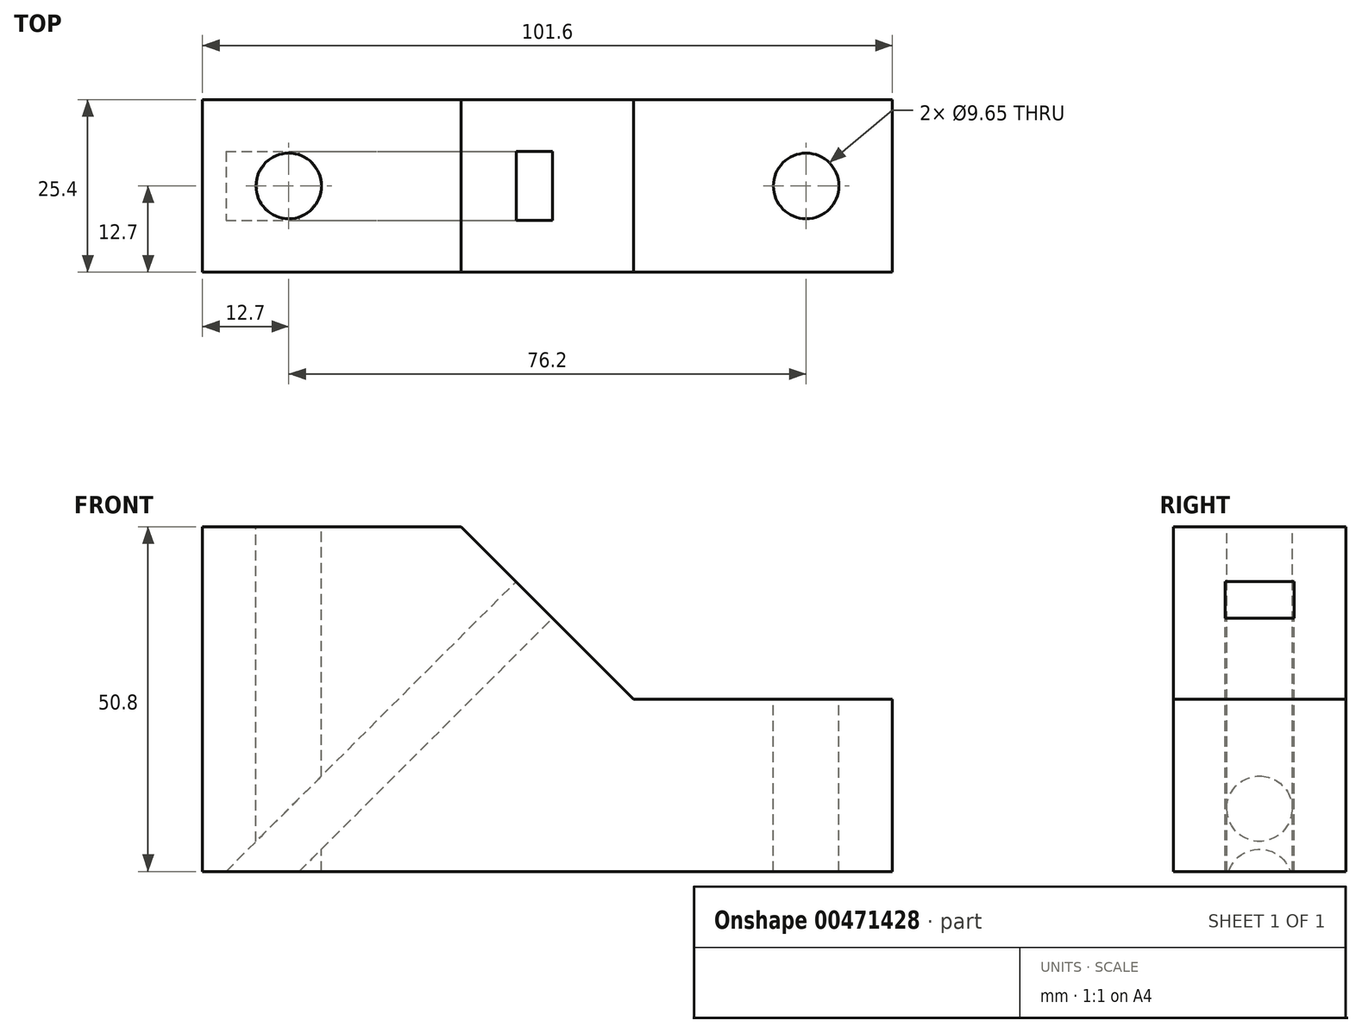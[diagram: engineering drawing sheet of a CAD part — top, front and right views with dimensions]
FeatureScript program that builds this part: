
annotation { "Feature Type Name" : "Feature", "Feature Type Description" : "" }
export const myFeature = defineFeature(function(context is Context, id is Id, definition is map)
    precondition{}
    {
        {
            var Q0;
            Q0=qCreatedBy(makeId("Front.planeOp"),FACE);
            var sketch = newSketch(context, id + "F0", { "sketchPlane" : qUnion([Q0])});
            skLineSegment(sketch, "E0", {"start": v(0, 0) * mm, "end": v(0, -50.8) * mm});
            skLineSegment(sketch, "E1", {"start": v(0, -50.8) * mm, "end": v(101.6, -50.8) * mm});
            skLineSegment(sketch, "E2", {"start": v(101.6, -50.8) * mm, "end": v(101.6, -25.4) * mm});
            skLineSegment(sketch, "E3", {"start": v(0, 0) * mm, "end": v(38.1, 0) * mm});
            skLineSegment(sketch, "E4", {"start": v(101.6, -25.4) * mm, "end": v(63.5, -25.4) * mm});
            skLineSegment(sketch, "E5", {"start": v(63.5, -25.4) * mm, "end": v(38.1, 0) * mm});
            skSolve(sketch);
        }
        {
            var Q0;
            Q0=makeQuery(id+"F0.imprint","IMPRINT",FACE,{"disambiguationData":[TD([[makeQuery(id+"F0.imprint","IMPRINT",EDGE,{"derivedFrom":sQuery(id+"F0.wireOp",EDGE,"E0")}),1.0]])]});
            extrude(context, id + "F1", {"entities" : qUnion([Q0]), "depth" : 25.4 * mm});
        }
        {
            var Q0;
            Q0=makeQuery(id+"F1.opExtrude","SWEPT_FACE",FACE,{"disambiguationData":[OSD([sQuery(id+"F0.wireOp",EDGE,"E3")])]});
            var sketch = newSketch(context, id + "F2", { "sketchPlane" : qUnion([Q0])});
            skPoint(sketch, "E6.centerSnap0", {"position": v(19.05, 0) * mm});
            skLineSegment(sketch, "E7", {"start": v(0, -12.7) * mm, "end": v(12.7, -12.7) * mm});
            skCircle(sketch, "E8", {"center": v(12.7, -12.7) * mm, "radius": 4.83 * mm});
            skSolve(sketch);
        }
        {
            var Q0;
            Q0 = qSketchRegion(id + "F2", true);
            extrude(context, id + "F3", {"entities" : qUnion([Q0]), "operationType" : NewBodyOperationType.REMOVE, "endBound" : BoundingType.THROUGH_ALL, "oppositeDirection" : true, "depth" : 25.4 * mm});
        }
        {
            var Q0;
            Q0=makeQuery(id+"F1.opExtrude","SWEPT_FACE",FACE,{"disambiguationData":[OSD([sQuery(id+"F0.wireOp",EDGE,"E4")])]});
            var sketch = newSketch(context, id + "F4", { "sketchPlane" : qUnion([Q0])});
            skCircle(sketch, "E9", {"center": v(88.9, -12.7) * mm, "radius": 4.83 * mm});
            skSolve(sketch);
        }
        {
            var Q0;
            Q0 = qSketchRegion(id + "F4", true);
            extrude(context, id + "F5", {"entities" : qUnion([Q0]), "operationType" : NewBodyOperationType.REMOVE, "endBound" : BoundingType.THROUGH_ALL, "oppositeDirection" : true, "depth" : 25.4 * mm});
        }
        {
            var Q0;
            Q0=makeQuery(id+"F1.opExtrude","SWEPT_FACE",FACE,{"disambiguationData":[OSD([sQuery(id+"F0.wireOp",EDGE,"E5")])]});
            var sketch = newSketch(context, id + "F6", { "sketchPlane" : qUnion([Q0])});
            skLineSegment(sketch, "E10", {"start": v(-7.62, -38.37) * mm, "end": v(-17.78, -38.37) * mm});
            skLineSegment(sketch, "E11", {"start": v(-17.78, -38.37) * mm, "end": v(-17.78, -46) * mm});
            skLineSegment(sketch, "E12", {"start": v(-7.62, -38.37) * mm, "end": v(-7.62, -46) * mm});
            skLineSegment(sketch, "E13", {"start": v(-7.62, -46) * mm, "end": v(-17.78, -46) * mm});
            skSolve(sketch);
        }
        {
            var Q0;
            Q0=makeQuery(id+"F6.imprint","IMPRINT",FACE,{"disambiguationData":[TD([[makeQuery(id+"F6.imprint","IMPRINT",EDGE,{"derivedFrom":sQuery(id+"F6.wireOp",EDGE,"E10")}),1.0]])]});
            extrude(context, id + "F7", {"entities" : qUnion([Q0]), "operationType" : NewBodyOperationType.REMOVE, "endBound" : BoundingType.THROUGH_ALL, "oppositeDirection" : true, "depth" : 25.4 * mm});
        }
    });
